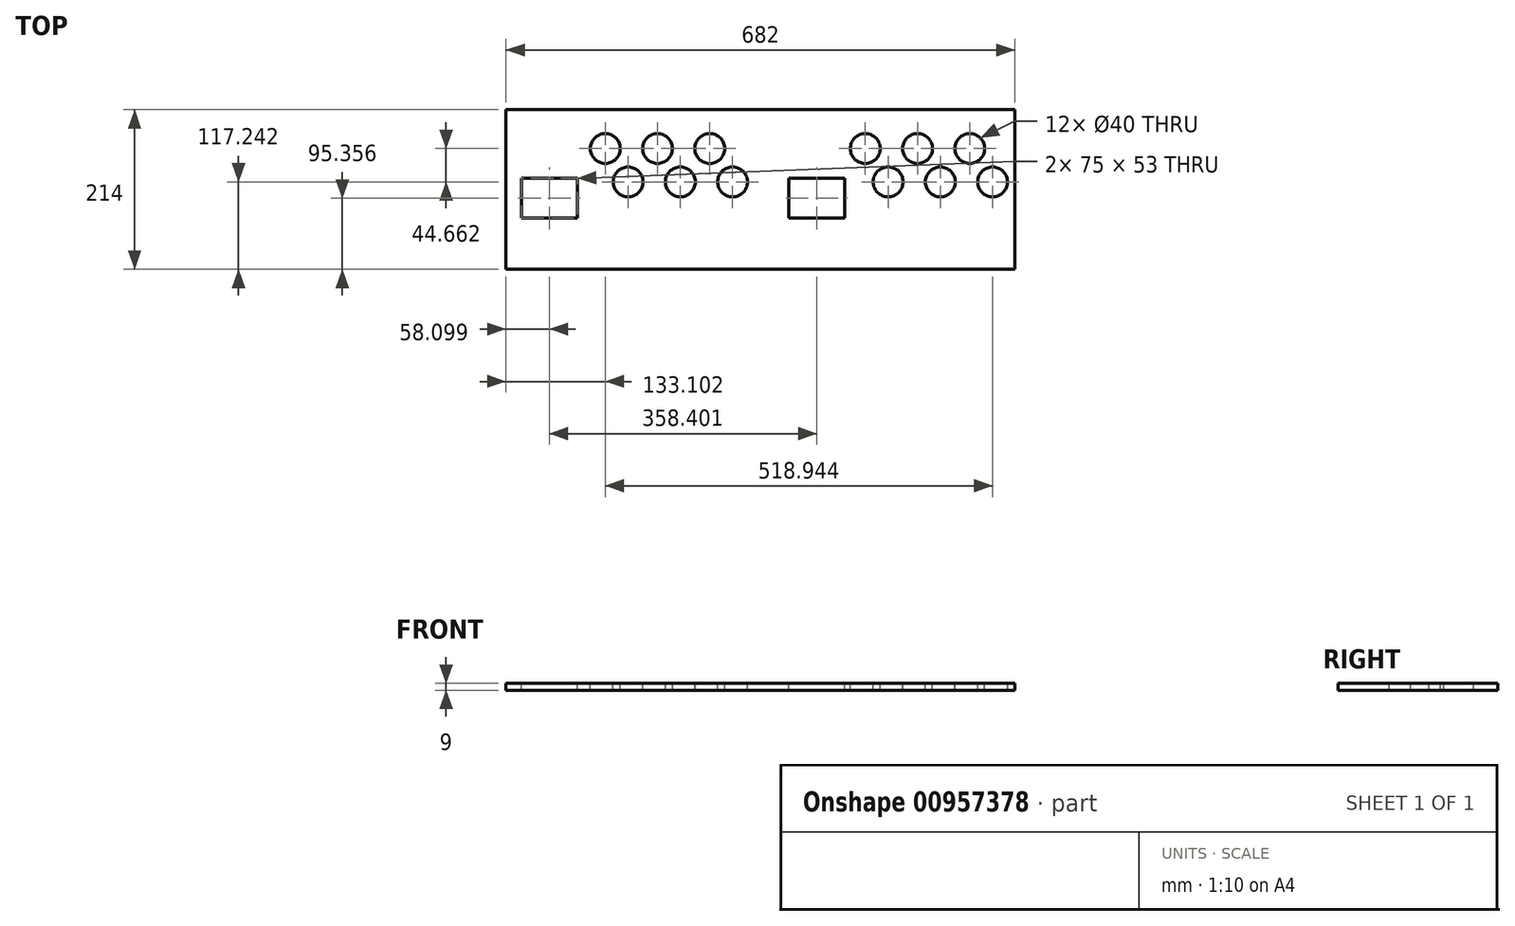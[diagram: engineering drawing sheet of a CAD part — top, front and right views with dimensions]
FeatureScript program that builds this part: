
annotation { "Feature Type Name" : "Feature", "Feature Type Description" : "" }
export const myFeature = defineFeature(function(context is Context, id is Id, definition is map)
    precondition{}
    {
        {
            var Q0;
            Q0=qCreatedBy(makeId("Top.planeOp"),FACE);
            var sketch = newSketch(context, id + "F0", { "sketchPlane" : qUnion([Q0])});
            skLineSegment(sketch, "E0.bottom", {"start": v(341, 107) * mm, "end": v(-341, 107) * mm});
            skLineSegment(sketch, "E0.top", {"start": v(341, -107) * mm, "end": v(-341, -107) * mm});
            skLineSegment(sketch, "E0.left", {"start": v(341, 107) * mm, "end": v(341, -107) * mm});
            skLineSegment(sketch, "E0.right", {"start": v(-341, 107) * mm, "end": v(-341, -107) * mm});
            skPoint(sketch, "E0.middle", {"position": v(0, 0) * mm});
            skSolve(sketch);
        }
        {
            var Q0;
            Q0=makeQuery(id+"F0.imprint","IMPRINT",FACE,{"disambiguationData":[TD([[makeQuery(id+"F0.imprint","IMPRINT",EDGE,{"derivedFrom":sQuery(id+"F0.wireOp",EDGE,"E0.bottom")}),1.0]])]});
            extrude(context, id + "F1", {"entities" : qUnion([Q0]), "depth" : 9 * mm, "offsetDistance" : 25 * mm});
        }
        {
            var Q0;
            Q0=makeQuery(id+"F1.opExtrude","CAP_FACE",FACE,{"disambiguationData":[OSD([sQuery(id+"F0.wireOp",EDGE,"E0.bottom"),sQuery(id+"F0.wireOp",EDGE,"E0.top"),sQuery(id+"F0.wireOp",EDGE,"E0.left"),sQuery(id+"F0.wireOp",EDGE,"E0.right")])],"isStart":false});
            var sketch = newSketch(context, id + "F2", { "sketchPlane" : qUnion([Q0])});
            skCircle(sketch, "E1", {"center": v(-207.9, 54.9) * mm, "radius": 20 * mm});
            skCircle(sketch, "E2", {"center": v(-137.9, 54.9) * mm, "radius": 20 * mm});
            skCircle(sketch, "E3", {"center": v(-67.9, 54.9) * mm, "radius": 20 * mm});
            skLineSegment(sketch, "E4.bottom", {"start": v(-245.4, 14.86) * mm, "end": v(-320.4, 14.86) * mm});
            skLineSegment(sketch, "E4.top", {"start": v(-245.4, -38.14) * mm, "end": v(-320.4, -38.14) * mm});
            skLineSegment(sketch, "E4.left", {"start": v(-245.4, 14.86) * mm, "end": v(-245.4, -38.14) * mm});
            skLineSegment(sketch, "E4.right", {"start": v(-320.4, 14.86) * mm, "end": v(-320.4, -38.14) * mm});
            skPoint(sketch, "E5", {"position": v(-320.4, -11.64) * mm});
            skCircle(sketch, "E6", {"center": v(-177.33, 10.24) * mm, "radius": 20 * mm});
            skCircle(sketch, "E7", {"center": v(-107.33, 10.24) * mm, "radius": 20 * mm});
            skCircle(sketch, "E8", {"center": v(-37.33, 10.24) * mm, "radius": 20 * mm});
            skCircle(sketch, "E9", {"center": v(140.48, 54.9) * mm, "radius": 20 * mm});
            skCircle(sketch, "E10", {"center": v(210.48, 54.9) * mm, "radius": 20 * mm});
            skCircle(sketch, "E11", {"center": v(280.48, 54.9) * mm, "radius": 20 * mm});
            skCircle(sketch, "E12", {"center": v(171.05, 10.24) * mm, "radius": 20 * mm});
            skCircle(sketch, "E13", {"center": v(241.05, 10.24) * mm, "radius": 20 * mm});
            skCircle(sketch, "E14", {"center": v(311.05, 10.24) * mm, "radius": 20 * mm});
            skLineSegment(sketch, "E15.bottom", {"start": v(113, 14.86) * mm, "end": v(38, 14.86) * mm});
            skLineSegment(sketch, "E15.top", {"start": v(113, -38.14) * mm, "end": v(38, -38.14) * mm});
            skLineSegment(sketch, "E15.left", {"start": v(113, 14.86) * mm, "end": v(113, -38.14) * mm});
            skLineSegment(sketch, "E15.right", {"start": v(38, 14.86) * mm, "end": v(38, -38.14) * mm});
            skPoint(sketch, "E16", {"position": v(38, -11.64) * mm});
            skSolve(sketch);
        }
        {
            var Q0;
            Q0 = qSketchRegion(id + "F2", true);
            extrude(context, id + "F3", {"entities" : qUnion([Q0]), "operationType" : NewBodyOperationType.REMOVE, "oppositeDirection" : true, "depth" : 25 * mm, "offsetDistance" : 25 * mm});
        }
    });
